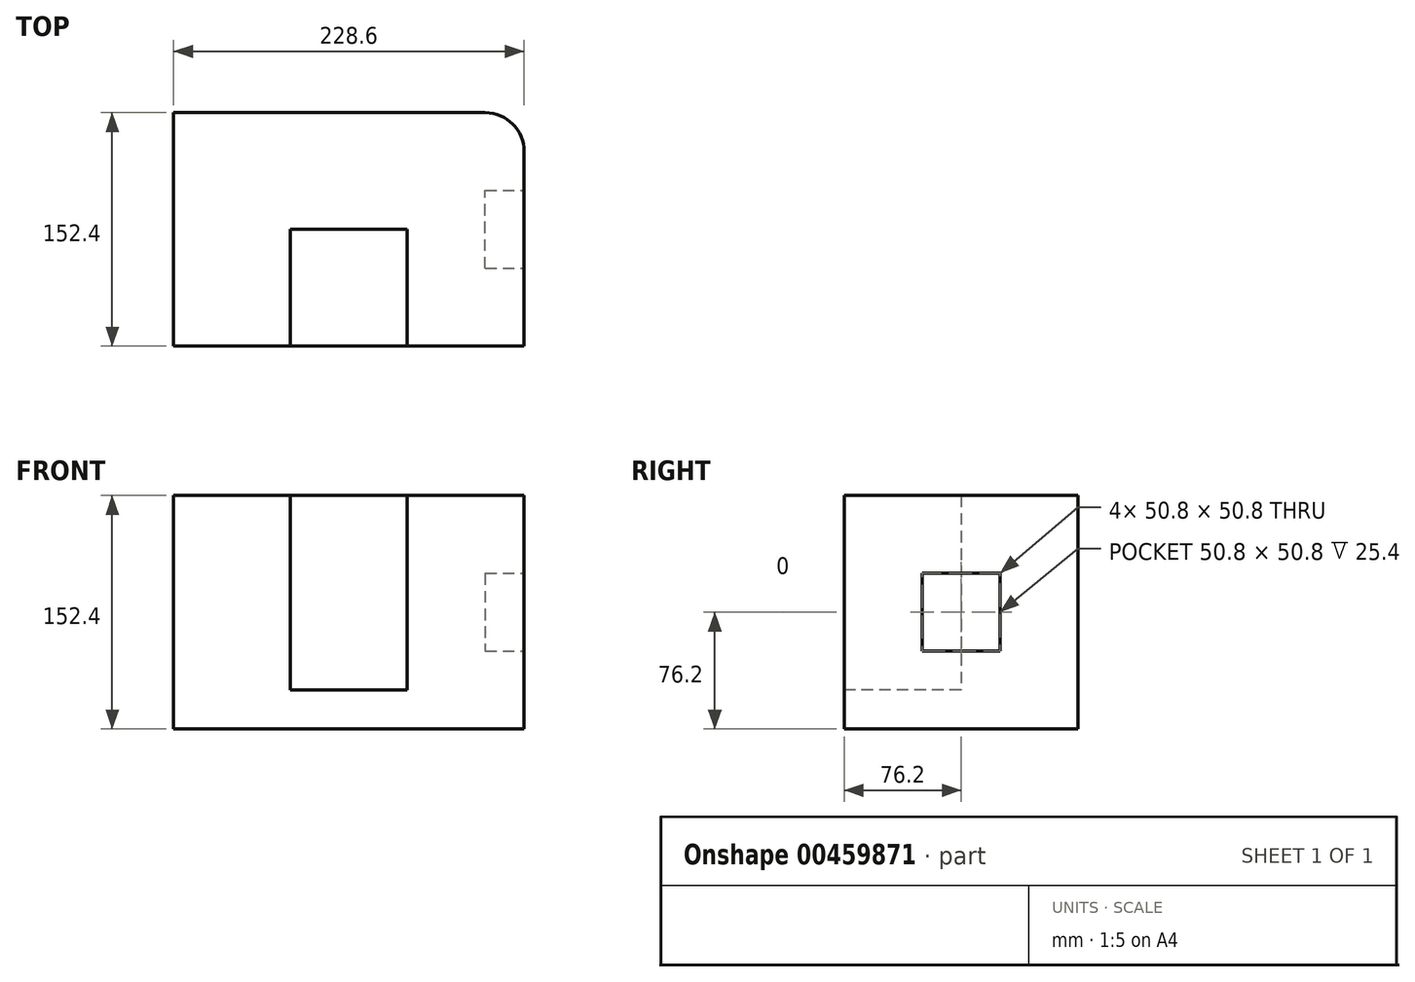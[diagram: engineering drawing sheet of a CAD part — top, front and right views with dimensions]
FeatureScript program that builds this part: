
annotation { "Feature Type Name" : "Feature", "Feature Type Description" : "" }
export const myFeature = defineFeature(function(context is Context, id is Id, definition is map)
    precondition{}
    {
        {
            var Q0;
            Q0=qCreatedBy(makeId("Front.planeOp"),FACE);
            var sketch = newSketch(context, id + "F0", { "sketchPlane" : qUnion([Q0])});
            skLineSegment(sketch, "E0", {"start": v(0, 0) * mm, "end": v(-228.6, 0) * mm});
            skLineSegment(sketch, "E1", {"start": v(-228.6, 0) * mm, "end": v(-228.6, 152.4) * mm});
            skLineSegment(sketch, "E2", {"start": v(-228.6, 152.4) * mm, "end": v(0, 152.4) * mm});
            skLineSegment(sketch, "E3", {"start": v(0, 152.4) * mm, "end": v(0, 0) * mm});
            skSolve(sketch);
        }
        {
            var Q0;
            Q0=makeQuery(id+"F0.imprint","IMPRINT",FACE,{"disambiguationData":[TD([[makeQuery(id+"F0.imprint","IMPRINT",EDGE,{"derivedFrom":sQuery(id+"F0.wireOp",EDGE,"E0")}),-1.0]])]});
            extrude(context, id + "F1", {"entities" : qUnion([Q0]), "depth" : 152.4 * mm});
        }
        {
            var Q0;
            Q0=makeQuery(id+"F1.opExtrude","CAP_FACE",FACE,{"disambiguationData":[OSD([sQuery(id+"F0.wireOp",EDGE,"E0"),sQuery(id+"F0.wireOp",EDGE,"E1"),sQuery(id+"F0.wireOp",EDGE,"E2"),sQuery(id+"F0.wireOp",EDGE,"E3")])],"isStart":false});
            var sketch = newSketch(context, id + "F2", { "sketchPlane" : qUnion([Q0])});
            skLineSegment(sketch, "E4.bottom", {"start": v(-152.4, 152.4) * mm, "end": v(-76.2, 152.4) * mm});
            skLineSegment(sketch, "E4.top", {"start": v(-152.4, 25.4) * mm, "end": v(-76.2, 25.4) * mm});
            skLineSegment(sketch, "E4.left", {"start": v(-152.4, 152.4) * mm, "end": v(-152.4, 25.4) * mm});
            skLineSegment(sketch, "E4.right", {"start": v(-76.2, 152.4) * mm, "end": v(-76.2, 25.4) * mm});
            skSolve(sketch);
        }
        {
            var Q0;
            Q0=makeQuery(id+"F2.imprint","IMPRINT",FACE,{"disambiguationData":[TD([[makeQuery(id+"F2.imprint","IMPRINT",EDGE,{"derivedFrom":sQuery(id+"F2.wireOp",EDGE,"E4.bottom")}),-1.0]])]});
            extrude(context, id + "F3", {"entities" : qUnion([Q0]), "operationType" : NewBodyOperationType.REMOVE, "oppositeDirection" : true, "depth" : 76.2 * mm});
        }
        {
            var Q0;
            Q0=makeQuery(id+"F1.opExtrude","SWEPT_FACE",FACE,{"disambiguationData":[OSD([sQuery(id+"F0.wireOp",EDGE,"E3")])]});
            var sketch = newSketch(context, id + "F4", { "sketchPlane" : qUnion([Q0])});
            skLineSegment(sketch, "E5.bottom", {"start": v(-101.6, 101.6) * mm, "end": v(-50.8, 101.6) * mm});
            skLineSegment(sketch, "E5.top", {"start": v(-101.6, 50.8) * mm, "end": v(-50.8, 50.8) * mm});
            skLineSegment(sketch, "E5.left", {"start": v(-101.6, 101.6) * mm, "end": v(-101.6, 50.8) * mm});
            skLineSegment(sketch, "E5.right", {"start": v(-50.8, 101.6) * mm, "end": v(-50.8, 50.8) * mm});
            skSolve(sketch);
        }
        {
            var Q0;
            Q0=makeQuery(id+"F4.imprint","IMPRINT",FACE,{"disambiguationData":[TD([[makeQuery(id+"F4.imprint","IMPRINT",EDGE,{"derivedFrom":sQuery(id+"F4.wireOp",EDGE,"E5.bottom")}),-1.0]])]});
            extrude(context, id + "F5", {"entities" : qUnion([Q0]), "operationType" : NewBodyOperationType.REMOVE, "oppositeDirection" : true, "depth" : 25.4 * mm});
        }
        {
            var Q0;
            Q0=makeQuery(id+"F1.opExtrude","CAP_EDGE",EDGE,{"disambiguationData":[OSD([sQuery(id+"F0.wireOp",EDGE,"E3")])],"isStart":true});
            fillet(context, id + "F6", {"entities" : qUnion([Q0]), "radius" : 25.4 * mm, "tangentPropagation" : true, "allowEdgeOverflow" : false});
        }
    });
